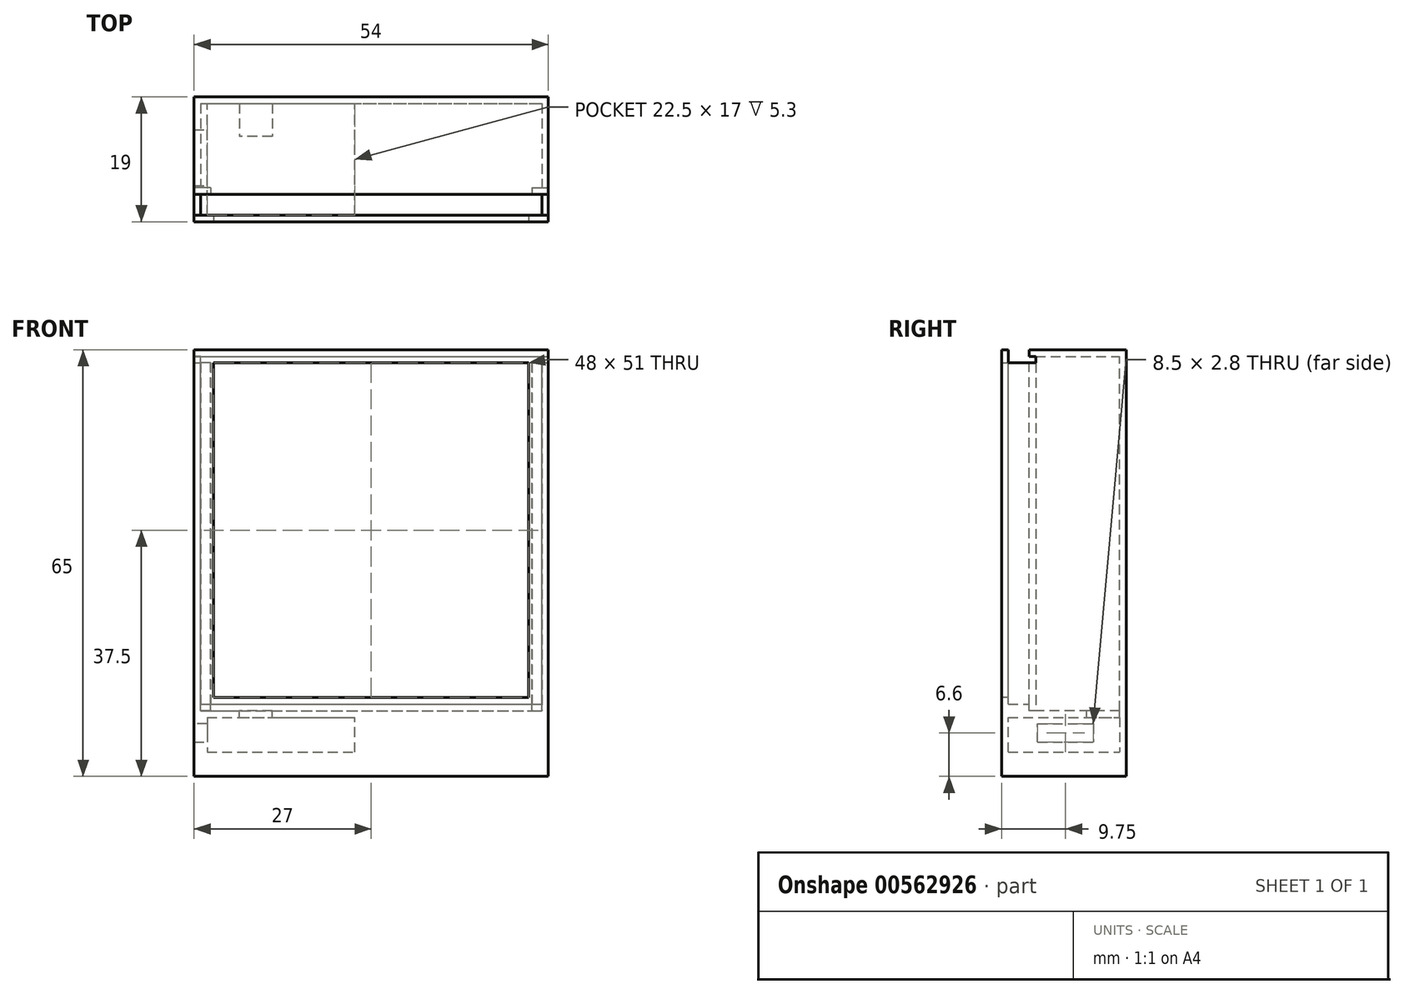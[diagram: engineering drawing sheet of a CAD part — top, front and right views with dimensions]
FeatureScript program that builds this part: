
annotation { "Feature Type Name" : "Feature", "Feature Type Description" : "" }
export const myFeature = defineFeature(function(context is Context, id is Id, definition is map)
    precondition{}
    {
        {
            var Q0;
            Q0=qCreatedBy(makeId("Top.planeOp"),FACE);
            var sketch = newSketch(context, id + "F0", { "sketchPlane" : qUnion([Q0])});
            skLineSegment(sketch, "E0.bottom", {"start": v(-27, 9.5) * mm, "end": v(27, 9.5) * mm});
            skLineSegment(sketch, "E0.top", {"start": v(-27, -9.5) * mm, "end": v(27, -9.5) * mm});
            skLineSegment(sketch, "E0.left", {"start": v(-27, 9.5) * mm, "end": v(-27, -9.5) * mm});
            skLineSegment(sketch, "E0.right", {"start": v(27, 9.5) * mm, "end": v(27, -9.5) * mm});
            skPoint(sketch, "E0.middle", {"position": v(0, 0) * mm});
            skSolve(sketch);
        }
        {
            var Q0;
            Q0=makeQuery(id+"F0.imprint","IMPRINT",FACE,{"disambiguationData":[TD([[makeQuery(id+"F0.imprint","IMPRINT",EDGE,{"derivedFrom":sQuery(id+"F0.wireOp",EDGE,"E0.bottom")}),-1.0]])]});
            extrude(context, id + "F1", {"entities" : qUnion([Q0]), "depth" : 10 * mm, "offsetDistance" : 25 * mm});
        }
        {
            var Q0;
            Q0=makeQuery(id+"F1.opExtrude","SWEPT_FACE",FACE,{"disambiguationData":[OSD([sQuery(id+"F0.wireOp",EDGE,"E0.right")])]});
            var sketch = newSketch(context, id + "F2", { "sketchPlane" : qUnion([Q0])});
            skLineSegment(sketch, "E1.bottom", {"start": v(-9.5, 10) * mm, "end": v(-8.5, 10) * mm});
            skLineSegment(sketch, "E1.top", {"start": v(-9.5, 63) * mm, "end": v(-8.5, 63) * mm});
            skLineSegment(sketch, "E1.left", {"start": v(-9.5, 10) * mm, "end": v(-9.5, 63) * mm});
            skLineSegment(sketch, "E1.right", {"start": v(-8.5, 10) * mm, "end": v(-8.5, 63) * mm});
            skLineSegment(sketch, "E2.bottom", {"start": v(9.5, 10) * mm, "end": v(8.5, 10) * mm});
            skLineSegment(sketch, "E2.top", {"start": v(9.5, 64) * mm, "end": v(8.5, 64) * mm});
            skLineSegment(sketch, "E2.left", {"start": v(9.5, 10) * mm, "end": v(9.5, 64) * mm});
            skLineSegment(sketch, "E2.right", {"start": v(8.5, 10) * mm, "end": v(8.5, 64) * mm});
            skLineSegment(sketch, "E3.bottom", {"start": v(-5.3, 10) * mm, "end": v(8.5, 10) * mm});
            skLineSegment(sketch, "E3.top", {"start": v(-5.3, 64) * mm, "end": v(8.5, 64) * mm});
            skLineSegment(sketch, "E3.left", {"start": v(-5.3, 10) * mm, "end": v(-5.3, 64) * mm});
            skLineSegment(sketch, "E4.bottom", {"start": v(9.5, 64) * mm, "end": v(-5.3, 64) * mm});
            skLineSegment(sketch, "E4.top", {"start": v(9.5, 65) * mm, "end": v(-5.3, 65) * mm});
            skLineSegment(sketch, "E4.left", {"start": v(9.5, 64) * mm, "end": v(9.5, 65) * mm});
            skLineSegment(sketch, "E4.right", {"start": v(-5.3, 64) * mm, "end": v(-5.3, 65) * mm});
            skLineSegment(sketch, "E5", {"start": v(-8.5, 11) * mm, "end": v(-5.3, 11) * mm});
            skLineSegment(sketch, "E6.bottom", {"start": v(-5.3, 64) * mm, "end": v(-4.3, 64) * mm});
            skLineSegment(sketch, "E6.left", {"start": v(-5.3, 64) * mm, "end": v(-5.3, 63) * mm});
            skLineSegment(sketch, "E7", {"start": v(-5.3, 63) * mm, "end": v(-4.3, 63) * mm});
            skLineSegment(sketch, "E8", {"start": v(-4.3, 63) * mm, "end": v(-4.3, 64) * mm});
            skLineSegment(sketch, "E9", {"start": v(-9.5, 63) * mm, "end": v(-9.5, 65) * mm});
            skLineSegment(sketch, "E10", {"start": v(-9.5, 65) * mm, "end": v(-8.5, 65) * mm});
            skLineSegment(sketch, "E11", {"start": v(-8.5, 65) * mm, "end": v(-8.5, 63) * mm});
            skLineSegment(sketch, "E12", {"start": v(-8.5, 63) * mm, "end": v(-5.3, 63) * mm});
            skLineSegment(sketch, "E13", {"start": v(-4.3, 63) * mm, "end": v(-4.3, 10) * mm});
            skLineSegment(sketch, "E14", {"start": v(-8.5, 12) * mm, "end": v(-9.5, 12) * mm});
            skSolve(sketch);
        }
        {
            var Q0;
            {var subQ0=sQuery(id+"F2.wireOp",EDGE,"E1.top");Q0=makeQuery(id+"F2.imprint","IMPRINT",FACE,{"disambiguationData":[TD([[makeQuery(id+"F2.imprint","IMPRINT",EDGE,{"derivedFrom":subQ0}),-1.0]])]});}
            var Q1;
            {var subQ0=sQuery(id+"F2.wireOp",EDGE,"E1.bottom");Q1=makeQuery(id+"F2.imprint","IMPRINT",FACE,{"disambiguationData":[TD([[makeQuery(id+"F2.imprint","IMPRINT",EDGE,{"derivedFrom":subQ0}),-1.0]])]});}
            extrude(context, id + "F3", {"entities" : qUnion([Q0, Q1]), "operationType" : NewBodyOperationType.ADD, "oppositeDirection" : true, "depth" : 3 * mm, "offsetDistance" : 25 * mm});
        }
        {
            var Q0;
            {var subQ3=sQuery(id+"F2.wireOp",EDGE,"E3.bottom");Q0=makeQuery(id+"F2.imprint","IMPRINT",FACE,{"disambiguationData":[TD([[makeQuery(id+"F2.imprint","IMPRINT",EDGE,{"derivedFrom":subQ3}),-1.0]])]});}
            var Q1;
            Q1=makeQuery(id+"F2.imprint","IMPRINT",FACE,{"disambiguationData":[TD([[makeQuery(id+"F2.imprint","IMPRINT",EDGE,{"derivedFrom":sQuery(id+"F2.wireOp",EDGE,"E6.bottom")}),-1.0]])]});
            extrude(context, id + "F4", {"entities" : qUnion([Q0, Q1]), "operationType" : NewBodyOperationType.ADD, "oppositeDirection" : true, "depth" : 1 * mm, "offsetDistance" : 25 * mm});
        }
        {
            var Q0;
            Q0=makeQuery(id+"F2.imprint","IMPRINT",FACE,{"disambiguationData":[TD([[makeQuery(id+"F2.imprint","IMPRINT",EDGE,{"derivedFrom":sQuery(id+"F2.wireOp",EDGE,"E2.bottom")}),-1.0]])]});
            var Q1;
            Q1=makeQuery(id+"F2.imprint","IMPRINT",FACE,{"disambiguationData":[TD([[makeQuery(id+"F2.imprint","IMPRINT",EDGE,{"derivedFrom":sQuery(id+"F2.wireOp",EDGE,"E4.top")}),1.0]])]});
            var Q2;
            Q2=makeQuery(id+"F1.opExtrude","SWEPT_FACE",FACE,{"disambiguationData":[OSD([sQuery(id+"F0.wireOp",EDGE,"E0.left")])]});
            extrude(context, id + "F5", {"entities" : qUnion([Q0, Q1]), "operationType" : NewBodyOperationType.ADD, "endBound" : BoundingType.UP_TO_SURFACE, "oppositeDirection" : true, "depth" : 50 * mm, "endBoundEntityFace" : qUnion([Q2]), "offsetDistance" : 25 * mm});
        }
        {
            var Q0;
            {var subQ2=sQuery(id+"F2.wireOp",EDGE,"E5");Q0=makeQuery(id+"F2.imprint","IMPRINT",FACE,{"disambiguationData":[TD([[makeQuery(id+"F2.imprint","IMPRINT",EDGE,{"derivedFrom":subQ2}),1.0]])]});}
            var Q1;
            {var subQ3=sQuery(id+"F2.wireOp",EDGE,"E5");Q1=makeQuery(id+"F2.imprint","IMPRINT",FACE,{"disambiguationData":[TD([[makeQuery(id+"F2.imprint","IMPRINT",EDGE,{"derivedFrom":subQ3}),-1.0]])]});}
            extrude(context, id + "F6", {"entities" : qUnion([Q0, Q1]), "operationType" : NewBodyOperationType.ADD, "oppositeDirection" : true, "depth" : 1 * mm, "offsetDistance" : 25 * mm});
        }
        {
            var Q0;
            {var subQ3=sQuery(id+"F2.wireOp",EDGE,"E5");Q0=makeQuery(id+"F2.imprint","IMPRINT",FACE,{"disambiguationData":[TD([[makeQuery(id+"F2.imprint","IMPRINT",EDGE,{"derivedFrom":subQ3}),-1.0]])]});}
            var Q1;
            {var subQ0=sQuery(id+"F2.wireOp",EDGE,"E1.bottom");Q1=makeQuery(id+"F2.imprint","IMPRINT",FACE,{"disambiguationData":[TD([[makeQuery(id+"F2.imprint","IMPRINT",EDGE,{"derivedFrom":subQ0}),-1.0]])]});}
            var Q2;
            Q2=makeQuery(id+"F2.imprint","IMPRINT",FACE,{"disambiguationData":[TD([[makeQuery(id+"F2.imprint","IMPRINT",EDGE,{"derivedFrom":sQuery(id+"F2.wireOp",EDGE,"E6.bottom")}),-1.0]])]});
            var Q3;
            Q3=makeQuery(id+"F2.imprint","IMPRINT",FACE,{"disambiguationData":[TD([[makeQuery(id+"F2.imprint","IMPRINT",EDGE,{"derivedFrom":sQuery(id+"F2.wireOp",EDGE,"E1.top")}),1.0]])]});
            var Q4;
            {var subQ0=sQuery(id+"F2.wireOp",EDGE,"E4.bottom");var subQ1=sQuery(id+"F2.wireOp",EDGE,"E2.right");var subQ2=sQuery(id+"F0.wireOp",EDGE,"E0.left");Q4=makeQuery(id+"F9.boolean.opBoolean","MERGE",FACE,{"derivedFrom":[makeQuery(id+"F5.boolean.opBoolean","MERGE",FACE,{"derivedFrom":[makeQuery(id+"F1.opExtrude","SWEPT_FACE",FACE,{"disambiguationData":[OSD([subQ2])]}),makeQuery(id+"F5.opExtrude","CAP_FACE",FACE,{"disambiguationData":[OSD([subQ2])],"isStart":false})]}),makeQuery(id+"F9.opPattern","COPY",FACE,{"derivedFrom":makeQuery(id+"F5.boolean.opBoolean","MERGE",FACE,{"derivedFrom":[makeQuery(id+"F4.boolean.opBoolean","MERGE",FACE,{"derivedFrom":[makeQuery(id+"F3.boolean.opBoolean","MERGE",FACE,{"derivedFrom":[makeQuery(id+"F1.opExtrude","SWEPT_FACE",FACE,{"disambiguationData":[OSD([sQuery(id+"F0.wireOp",EDGE,"E0.right")])]}),makeQuery(id+"F3.opExtrude","CAP_FACE",FACE,{"disambiguationData":[OSD([sQuery(id+"F2.wireOp",EDGE,"E1.bottom"),sQuery(id+"F2.wireOp",EDGE,"E1.top"),sQuery(id+"F2.wireOp",EDGE,"E1.left"),sQuery(id+"F2.wireOp",EDGE,"E1.right")])],"isStart":true})]}),makeQuery(id+"F4.opExtrude","CAP_FACE",FACE,{"disambiguationData":[OSD([sQuery(id+"F2.wireOp",EDGE,"E3.bottom"),sQuery(id+"F2.wireOp",EDGE,"E3.left"),subQ1,subQ0])],"isStart":true})]}),makeQuery(id+"F5.opExtrude","CAP_FACE",FACE,{"disambiguationData":[OSD([sQuery(id+"F2.wireOp",EDGE,"E2.bottom"),sQuery(id+"F2.wireOp",EDGE,"E2.left"),subQ1,subQ0,sQuery(id+"F2.wireOp",EDGE,"E4.top"),sQuery(id+"F2.wireOp",EDGE,"E4.left"),sQuery(id+"F2.wireOp",EDGE,"E4.right")])],"isStart":true})]}),"instanceName":"1"})]});}
            extrude(context, id + "F7", {"entities" : qUnion([Q0, Q1, Q2, Q3]), "operationType" : NewBodyOperationType.ADD, "endBound" : BoundingType.UP_TO_SURFACE, "oppositeDirection" : true, "depth" : 25 * mm, "endBoundEntityFace" : qUnion([Q4]), "offsetDistance" : 25 * mm});
        }
        {
            var Q0;
            {var subQ0=sQuery(id+"F2.wireOp",EDGE,"E7");Q0=makeQuery(id+"F2.imprint","IMPRINT",FACE,{"disambiguationData":[TD([[makeQuery(id+"F2.imprint","IMPRINT",EDGE,{"derivedFrom":subQ0}),-1.0]])]});}
            extrude(context, id + "F8", {"entities" : qUnion([Q0]), "operationType" : NewBodyOperationType.ADD, "oppositeDirection" : true, "depth" : 2.5 * mm, "offsetDistance" : 25 * mm});
        }
        {
            var Q0;
            Q0=makeQuery(id+"F1.opExtrude","SWEPT_BODY",BODY,{"disambiguationData":[OSD([sQuery(id+"F0.wireOp",EDGE,"E0.bottom"),sQuery(id+"F0.wireOp",EDGE,"E0.top"),sQuery(id+"F0.wireOp",EDGE,"E0.left"),sQuery(id+"F0.wireOp",EDGE,"E0.right")])]});
            var Q1;
            Q1=qCreatedBy(makeId("Right.planeOp"),FACE);
            mirror(context, id + "F9", {"operationType" : NewBodyOperationType.ADD, "entities" : qUnion([Q0]), "mirrorPlane" : qUnion([Q1])});
        }
        {
            var Q0;
            Q0=makeQuery(id+"F5.boolean.opBoolean","MERGE",FACE,{"derivedFrom":[makeQuery(id+"F1.opExtrude","SWEPT_FACE",FACE,{"disambiguationData":[OSD([sQuery(id+"F0.wireOp",EDGE,"E0.bottom")])]}),makeQuery(id+"F5.opExtrude","SWEPT_FACE",FACE,{"disambiguationData":[OSD([sQuery(id+"F2.wireOp",EDGE,"E2.left"),sQuery(id+"F2.wireOp",EDGE,"E4.left")])]})]});
            var sketch = newSketch(context, id + "F10", { "sketchPlane" : qUnion([Q0])});
            skLineSegment(sketch, "E15", {"start": v(27, 5.2) * mm, "end": v(25, 5.2) * mm});
            skLineSegment(sketch, "E16", {"start": v(25, 5.2) * mm, "end": v(25, 3.7) * mm});
            skLineSegment(sketch, "E17", {"start": v(25, 3.7) * mm, "end": v(2.5, 3.7) * mm});
            skLineSegment(sketch, "E18", {"start": v(2.5, 3.7) * mm, "end": v(2.5, 8) * mm});
            skLineSegment(sketch, "E19", {"start": v(25, 8) * mm, "end": v(27, 8) * mm});
            skLineSegment(sketch, "E20", {"start": v(27, 8) * mm, "end": v(27, 5.2) * mm});
            skLineSegment(sketch, "E21", {"start": v(25, 8) * mm, "end": v(25, 9) * mm});
            skLineSegment(sketch, "E22", {"start": v(25, 9) * mm, "end": v(2.5, 9) * mm});
            skLineSegment(sketch, "E23", {"start": v(2.5, 9) * mm, "end": v(2.5, 8) * mm});
            skLineSegment(sketch, "E24", {"start": v(25, 8) * mm, "end": v(25, 5.2) * mm});
            skSolve(sketch);
        }
        {
            var Q0;
            Q0=makeQuery(id+"F10.imprint","IMPRINT",FACE,{"disambiguationData":[TD([[makeQuery(id+"F10.imprint","IMPRINT",EDGE,{"derivedFrom":sQuery(id+"F10.wireOp",EDGE,"E15")}),-1.0]])]});
            var Q1;
            Q1=makeQuery(id+"F10.imprint","IMPRINT",FACE,{"disambiguationData":[TD([[makeQuery(id+"F10.imprint","IMPRINT",EDGE,{"derivedFrom":sQuery(id+"F10.wireOp",EDGE,"E16")}),-1.0]])]});
            extrude(context, id + "F11", {"entities" : qUnion([Q0, Q1]), "operationType" : NewBodyOperationType.REMOVE, "oppositeDirection" : true, "depth" : 18 * mm, "offsetDistance" : 25 * mm});
        }
        {
            var Q0;
            Q0=makeQuery(id+"F11.boolean.opBoolean","COPY",FACE,{"derivedFrom":makeQuery(id+"F11.opExtrude","CAP_FACE",FACE,{"disambiguationData":[OSD([sQuery(id+"F10.wireOp",EDGE,"E15"),sQuery(id+"F10.wireOp",EDGE,"E16"),sQuery(id+"F10.wireOp",EDGE,"E17"),sQuery(id+"F10.wireOp",EDGE,"E18"),sQuery(id+"F10.wireOp",EDGE,"E19"),sQuery(id+"F10.wireOp",EDGE,"E20"),sQuery(id+"F10.wireOp",EDGE,"E21"),sQuery(id+"F10.wireOp",EDGE,"E22"),sQuery(id+"F10.wireOp",EDGE,"E23")])],"isStart":false})});
            var sketch = newSketch(context, id + "F12", { "sketchPlane" : qUnion([Q0])});
            skLineSegment(sketch, "E25.0.0", {"start": v(25, 5.2) * mm, "end": v(25, 8) * mm});
            skLineSegment(sketch, "E25.0.1", {"start": v(25, 8) * mm, "end": v(25, 9) * mm});
            skLineSegment(sketch, "E25.0.2", {"start": v(25, 9) * mm, "end": v(25, 9) * mm});
            skLineSegment(sketch, "E25.0.3", {"start": v(25, 9) * mm, "end": v(2.5, 9) * mm});
            skLineSegment(sketch, "E25.0.4", {"start": v(2.5, 9) * mm, "end": v(2.5, 8) * mm});
            skLineSegment(sketch, "E25.0.5", {"start": v(2.5, 8) * mm, "end": v(2.5, 3.7) * mm});
            skLineSegment(sketch, "E25.0.6", {"start": v(2.5, 3.7) * mm, "end": v(25, 3.7) * mm});
            skLineSegment(sketch, "E25.0.7", {"start": v(25, 3.7) * mm, "end": v(25, 5.2) * mm});
            skSolve(sketch);
        }
        {
            var Q0;
            Q0=makeQuery(id+"F12.imprint","IMPRINT",FACE,{"disambiguationData":[TD([[makeQuery(id+"F12.imprint","IMPRINT",EDGE,{"derivedFrom":sQuery(id+"F12.wireOp",EDGE,"E25.0.0")}),-1.0]])]});
            extrude(context, id + "F13", {"entities" : qUnion([Q0]), "operationType" : NewBodyOperationType.ADD, "depth" : 4.5 * mm, "offsetDistance" : 25 * mm});
        }
        {
            var Q0;
            Q0=makeQuery(id+"F10.imprint","IMPRINT",FACE,{"disambiguationData":[TD([[makeQuery(id+"F10.imprint","IMPRINT",EDGE,{"derivedFrom":sQuery(id+"F10.wireOp",EDGE,"E16")}),-1.0]])]});
            var Q1;
            {var subQ0=sQuery(id+"F10.wireOp",EDGE,"yeTjEzG5-JwYW-sSWF-ZSfb-bieZ8j3D3AQw");Q1=makeQuery(id+"F10.imprint","IMPRINT",FACE,{"disambiguationData":[TD([[makeQuery(id+"F10.imprint","IMPRINT",EDGE,{"derivedFrom":subQ0}),1.0]])]});}
            extrude(context, id + "F14", {"entities" : qUnion([Q0, Q1]), "oppositeDirection" : true, "depth" : 1 * mm, "offsetDistance" : 25 * mm});
        }
        {
            var Q0;
            Q0=makeQuery(id+"F10.imprint","IMPRINT",FACE,{"disambiguationData":[TD([[makeQuery(id+"F10.imprint","IMPRINT",EDGE,{"derivedFrom":sQuery(id+"F10.wireOp",EDGE,"E15")}),-1.0]])]});
            extrude(context, id + "F15", {"entities" : qUnion([Q0]), "operationType" : NewBodyOperationType.ADD, "oppositeDirection" : true, "depth" : 5 * mm, "offsetDistance" : 25 * mm});
        }
        {
            var Q0;
            Q0=makeQuery(id+"F1.opExtrude","CAP_FACE",FACE,{"disambiguationData":[OSD([sQuery(id+"F0.wireOp",EDGE,"E0.bottom"),sQuery(id+"F0.wireOp",EDGE,"E0.top"),sQuery(id+"F0.wireOp",EDGE,"E0.left"),sQuery(id+"F0.wireOp",EDGE,"E0.right")])],"isStart":false});
            var sketch = newSketch(context, id + "F16", { "sketchPlane" : qUnion([Q0])});
            skLineSegment(sketch, "E26.bottom", {"start": v(-15.07, 8.5) * mm, "end": v(-20.07, 8.5) * mm});
            skLineSegment(sketch, "E26.top", {"start": v(-15.07, 3.5) * mm, "end": v(-20.07, 3.5) * mm});
            skLineSegment(sketch, "E26.left", {"start": v(-15.07, 8.5) * mm, "end": v(-15.07, 3.5) * mm});
            skLineSegment(sketch, "E26.right", {"start": v(-20.07, 8.5) * mm, "end": v(-20.07, 3.5) * mm});
            skSolve(sketch);
        }
        {
            var Q0;
            Q0=makeQuery(id+"F16.imprint","IMPRINT",FACE,{"disambiguationData":[TD([[makeQuery(id+"F16.imprint","IMPRINT",EDGE,{"derivedFrom":sQuery(id+"F16.wireOp",EDGE,"E26.bottom")}),-1.0]])]});
            extrude(context, id + "F17", {"entities" : qUnion([Q0]), "operationType" : NewBodyOperationType.REMOVE, "endBound" : BoundingType.UP_TO_NEXT, "oppositeDirection" : true, "depth" : 25 * mm, "offsetDistance" : 25 * mm});
        }
    });
